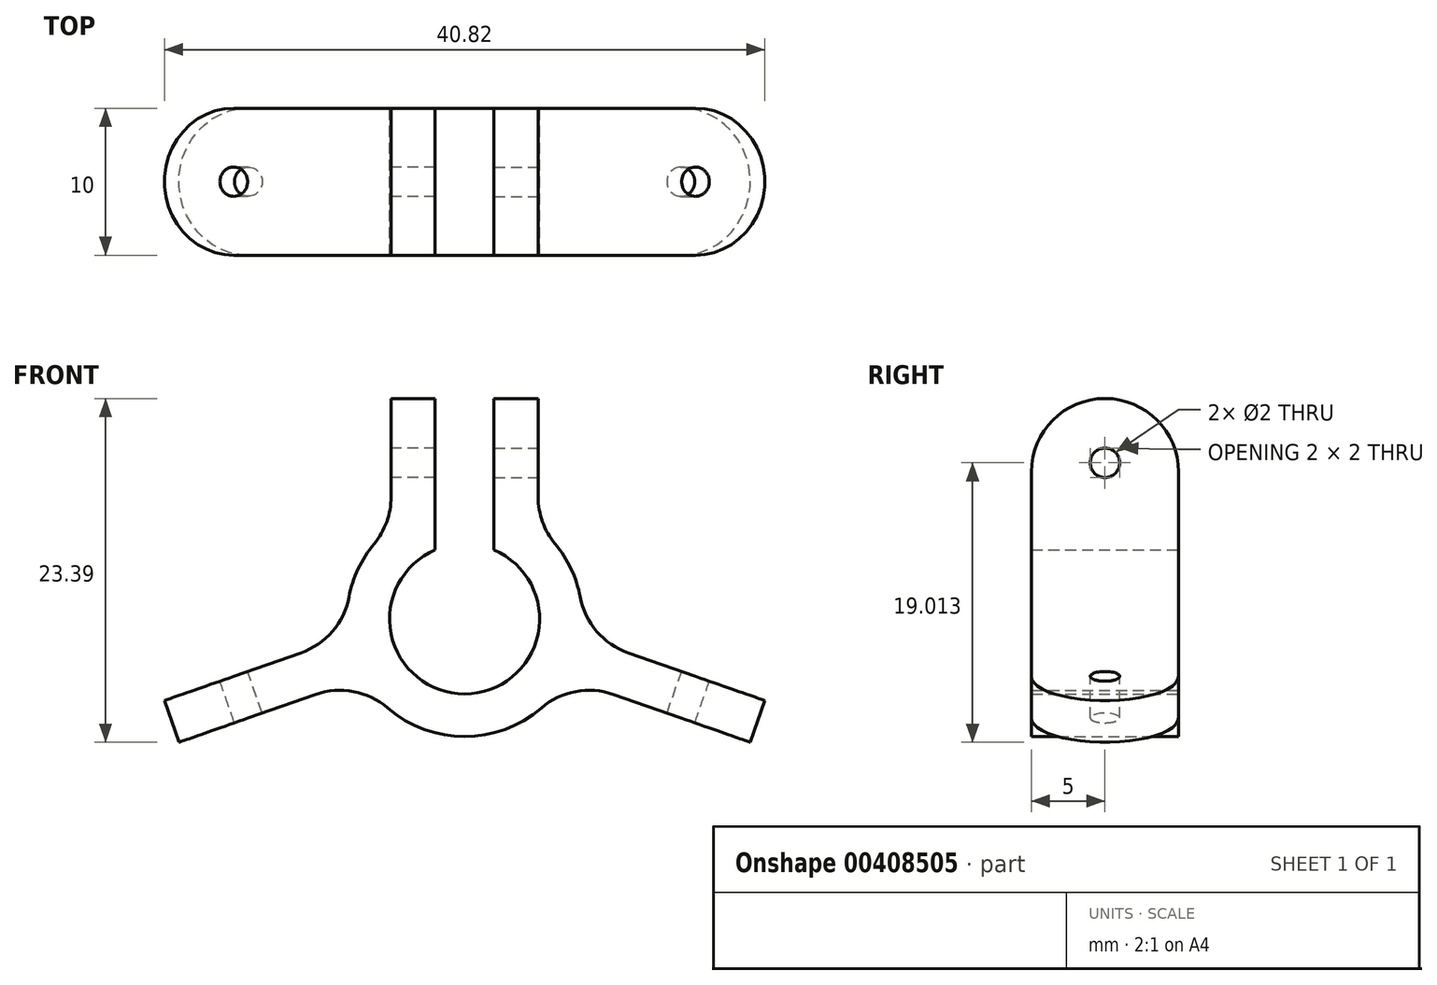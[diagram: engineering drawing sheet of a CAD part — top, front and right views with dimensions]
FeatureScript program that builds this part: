
annotation { "Feature Type Name" : "Feature", "Feature Type Description" : "" }
export const myFeature = defineFeature(function(context is Context, id is Id, definition is map)
    precondition{}
    {
        {
            var Q0;
            Q0=qCreatedBy(makeId("Front.planeOp"),FACE);
            var sketch = newSketch(context, id + "F0", { "sketchPlane" : qUnion([Q0])});
            skArc(sketch, "E0", {"start": v(0, -5.1) * mm, "mid": v(5, -1.02) * mm, "end": v(2, 4.7) * mm});
            skLineSegment(sketch, "E1", {"start": v(0, 0) * mm, "end": v(24.9, -8.72) * mm, "construction": true});
            skLineSegment(sketch, "E2", {"start": v(4.1, -3.03) * mm, "end": v(19.42, -8.39) * mm});
            skLineSegment(sketch, "E3", {"start": v(19.42, -8.39) * mm, "end": v(20.41, -5.56) * mm});
            skLineSegment(sketch, "E4", {"start": v(20.41, -5.56) * mm, "end": v(5.1, -0.2) * mm});
            skLineSegment(sketch, "E5", {"start": v(5, 15) * mm, "end": v(5, 6.24) * mm});
            skLineSegment(sketch, "E6", {"start": v(2, 4.7) * mm, "end": v(2, 15) * mm});
            skLineSegment(sketch, "E7.trimOffspring", {"start": v(2, 15) * mm, "end": v(5, 15) * mm});
            skLineSegment(sketch, "E8", {"start": v(0, 15) * mm, "end": v(0, -19.29) * mm, "construction": true});
            skArc(sketch, "E9.trimOffspring", {"start": v(0, -8) * mm, "mid": v(7.94, -1) * mm, "end": v(2, 7.75) * mm});
            skLineSegment(sketch, "E10", {"start": v(0, -5.1) * mm, "end": v(0, -8) * mm});
            skSolve(sketch);
        }
        {
            var Q0;
            {var subQ4=sQuery(id+"F0.wireOp",EDGE,"E6");var subQ6=sQuery(id+"F0.wireOp",EDGE,"E0");var subQ8=makeQuery(id+"F0.imprint","INTERSECT",VERTEX,{"derivedFrom":[subQ6,subQ4]});Q0=makeQuery(id+"F0.imprint","IMPRINT",FACE,{"disambiguationData":[TD([[makeQuery(id+"F0.imprint","IMPRINT",EDGE,{"disambiguationData":[TD([[subQ8,1.0]])],"derivedFrom":subQ6}),-1.0]])]});}
            var Q1;
            {var subQ0=sQuery(id+"F0.wireOp",EDGE,"E2");var subQ1=sQuery(id+"F0.wireOp",EDGE,"E0");var subQ2=makeQuery(id+"F0.imprint","INTERSECT",VERTEX,{"derivedFrom":[subQ1,subQ0]});Q1=makeQuery(id+"F0.imprint","IMPRINT",FACE,{"disambiguationData":[TD([[makeQuery(id+"F0.imprint","IMPRINT",EDGE,{"disambiguationData":[TD([[subQ2,-1.0]])],"derivedFrom":subQ1}),-1.0]])]});}
            var Q2;
            {var subQ4=sQuery(id+"F0.wireOp",EDGE,"i9qYtkfv-SZLV-WTxb-UqVO-jSNCvkcmy04q");var subQ6=sQuery(id+"F0.wireOp",EDGE,"E0");var subQ8=makeQuery(id+"F0.imprint","INTERSECT",VERTEX,{"derivedFrom":[subQ6,subQ4]});Q2=makeQuery(id+"F0.imprint","IMPRINT",FACE,{"disambiguationData":[TD([[makeQuery(id+"F0.imprint","IMPRINT",EDGE,{"disambiguationData":[TD([[subQ8,-1.0]])],"derivedFrom":subQ6}),-1.0]])]});}
            var Q3;
            {var subQ3=sQuery(id+"F0.wireOp",EDGE,"g51z1Yhh-3KAa-QBzB-FuLV-YnATeuSFtZAR");Q3=makeQuery(id+"F0.imprint","IMPRINT",FACE,{"disambiguationData":[TD([[makeQuery(id+"F0.imprint","IMPRINT",EDGE,{"derivedFrom":subQ3}),-1.0]])]});}
            var Q4;
            {var subQ3=sQuery(id+"F0.wireOp",EDGE,"E5");Q4=makeQuery(id+"F0.imprint","IMPRINT",FACE,{"disambiguationData":[TD([[makeQuery(id+"F0.imprint","IMPRINT",EDGE,{"derivedFrom":subQ3}),-1.0]])]});}
            var Q5;
            {var subQ0=sQuery(id+"F0.wireOp",EDGE,"E3");Q5=makeQuery(id+"F0.imprint","IMPRINT",FACE,{"disambiguationData":[TD([[makeQuery(id+"F0.imprint","IMPRINT",EDGE,{"derivedFrom":subQ0}),1.0]])]});}
            extrude(context, id + "F1", {"entities" : qUnion([Q0, Q1, Q2, Q3, Q4, Q5]), "endBound" : BoundingType.SYMMETRIC, "depth" : 10 * mm});
        }
        {
            var Q0;
            Q0=makeQuery(id+"F1.opExtrude","SWEPT_FACE",FACE,{"disambiguationData":[OSD([sQuery(id+"F0.wireOp",EDGE,"E4")])]});
            var sketch = newSketch(context, id + "F2", { "sketchPlane" : qUnion([Q0])});
            skLineSegment(sketch, "E11", {"start": v(16.1, -5) * mm, "end": v(16.1, 5) * mm, "construction": true});
            skCircle(sketch, "E12", {"center": v(16.1, 0) * mm, "radius": 1 * mm});
            skSolve(sketch);
        }
        {
            var Q0;
            Q0=makeQuery(id+"F2.imprint","IMPRINT",FACE,{"disambiguationData":[TD([[makeQuery(id+"F2.imprint","IMPRINT",EDGE,{"derivedFrom":sQuery(id+"F2.wireOp",EDGE,"E12")}),1.0]])]});
            extrude(context, id + "F3", {"entities" : qUnion([Q0]), "operationType" : NewBodyOperationType.REMOVE, "oppositeDirection" : true, "depth" : 25 * mm});
        }
        {
            var Q0;
            Q0=makeQuery(id+"F1.opExtrude","SWEPT_FACE",FACE,{"disambiguationData":[OSD([sQuery(id+"F0.wireOp",EDGE,"E5")])]});
            var sketch = newSketch(context, id + "F4", { "sketchPlane" : qUnion([Q0])});
            skLineSegment(sketch, "E13", {"start": v(-5, 10.62) * mm, "end": v(5, 10.62) * mm, "construction": true});
            skLineSegment(sketch, "E14", {"start": v(0, 15) * mm, "end": v(0, 6.24) * mm, "construction": true});
            skCircle(sketch, "E15", {"center": v(0, 10.62) * mm, "radius": 1 * mm});
            skSolve(sketch);
        }
        {
            var Q0;
            Q0=qSketchRegion(id+"F4",true);
            extrude(context, id + "F5", {"entities" : qUnion([Q0]), "operationType" : NewBodyOperationType.REMOVE, "oppositeDirection" : true, "depth" : 25 * mm});
        }
        {
            var Q0;
            Q0=makeQuery(id+"F1.opExtrude","CAP_EDGE",EDGE,{"disambiguationData":[OSD([sQuery(id+"F0.wireOp",EDGE,"E3")])],"isStart":true});
            var Q1;
            Q1=makeQuery(id+"F1.opExtrude","CAP_EDGE",EDGE,{"disambiguationData":[OSD([sQuery(id+"F0.wireOp",EDGE,"E3")])],"isStart":false});
            var Q2;
            Q2=makeQuery(id+"F1.opExtrude","CAP_EDGE",EDGE,{"disambiguationData":[OSD([sQuery(id+"F0.wireOp",EDGE,"E7.trimOffspring")])],"isStart":false});
            var Q3;
            Q3=makeQuery(id+"F1.opExtrude","CAP_EDGE",EDGE,{"disambiguationData":[OSD([sQuery(id+"F0.wireOp",EDGE,"E7.trimOffspring")])],"isStart":true});
            fillet(context, id + "F6", {"entities" : qUnion([Q0, Q1, Q2, Q3]), "radius" : 5 * mm, "tangentPropagation" : true, "allowEdgeOverflow" : false});
        }
        {
            var Q0;
            Q0=makeQuery(id+"F1.opExtrude","SWEPT_EDGE",EDGE,{"disambiguationData":[OSD([sQuery(id+"F0.wireOp",EDGE,"E5"),sQuery(id+"F0.wireOp",EDGE,"E9.trimOffspring")])]});
            var Q1;
            Q1=makeQuery(id+"F1.opExtrude","SWEPT_EDGE",EDGE,{"disambiguationData":[OSD([sQuery(id+"F0.wireOp",EDGE,"E4"),sQuery(id+"F0.wireOp",EDGE,"E9.trimOffspring")])]});
            var Q2;
            Q2=makeQuery(id+"F1.opExtrude","SWEPT_EDGE",EDGE,{"disambiguationData":[OSD([sQuery(id+"F0.wireOp",EDGE,"E2"),sQuery(id+"F0.wireOp",EDGE,"E9.trimOffspring")])]});
            fillet(context, id + "F7", {"entities" : qUnion([Q0, Q1, Q2]), "radius" : 5 * mm, "tangentPropagation" : true, "allowEdgeOverflow" : false});
        }
        {
            var Q0;
            Q0=makeQuery(id+"F1.opExtrude","SWEPT_BODY",BODY,{"disambiguationData":[OSD([sQuery(id+"F0.wireOp",EDGE,"E0"),sQuery(id+"F0.wireOp",EDGE,"E2"),sQuery(id+"F0.wireOp",EDGE,"E3"),sQuery(id+"F0.wireOp",EDGE,"E4"),sQuery(id+"F0.wireOp",EDGE,"E5"),sQuery(id+"F0.wireOp",EDGE,"E6"),sQuery(id+"F0.wireOp",EDGE,"E7.trimOffspring"),sQuery(id+"F0.wireOp",EDGE,"E9.trimOffspring"),sQuery(id+"F0.wireOp",EDGE,"E10")])]});
            var Q1;
            Q1=qCreatedBy(makeId("Right.planeOp"),FACE);
            mirror(context, id + "F8", {"operationType" : NewBodyOperationType.ADD, "entities" : qUnion([Q0]), "mirrorPlane" : qUnion([Q1])});
        }
    });
